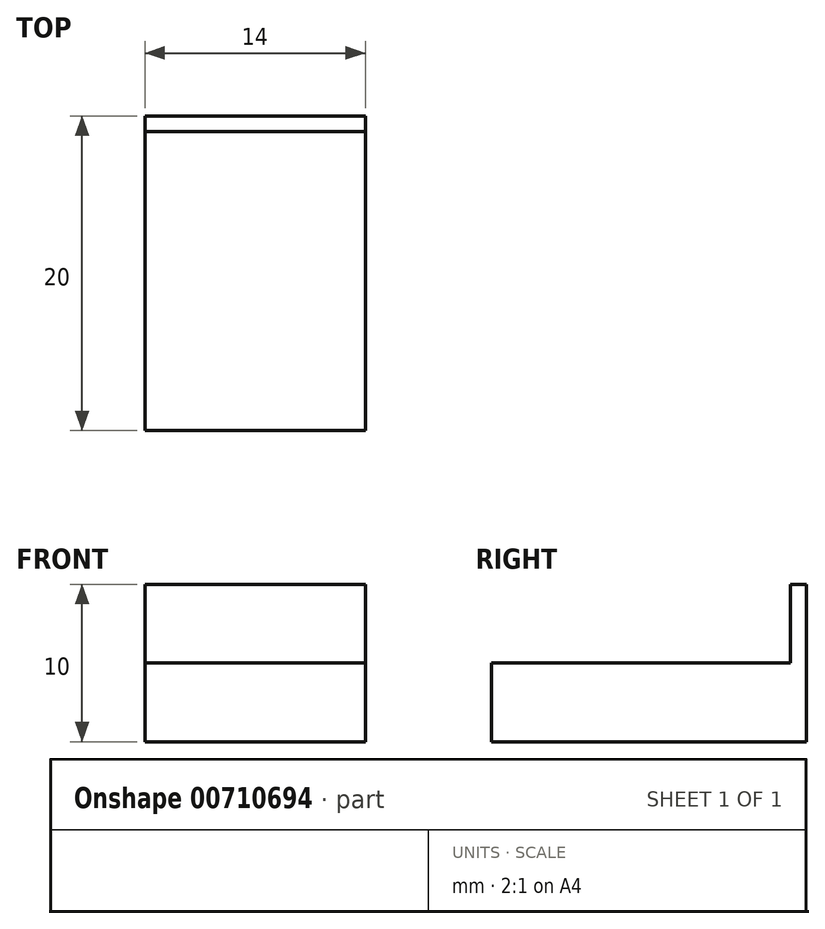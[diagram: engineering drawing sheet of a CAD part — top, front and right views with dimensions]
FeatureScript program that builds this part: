
annotation { "Feature Type Name" : "Feature", "Feature Type Description" : "" }
export const myFeature = defineFeature(function(context is Context, id is Id, definition is map)
    precondition{}
    {
        {
            var Q0;
            Q0=qCreatedBy(makeId("Top.planeOp"),FACE);
            var sketch = newSketch(context, id + "F0", { "sketchPlane" : qUnion([Q0])});
            skLineSegment(sketch, "E0.bottom", {"start": v(0, 0) * mm, "end": v(14, 0) * mm});
            skLineSegment(sketch, "E0.top", {"start": v(0, -20) * mm, "end": v(14, -20) * mm});
            skLineSegment(sketch, "E0.left", {"start": v(0, 0) * mm, "end": v(0, -20) * mm});
            skLineSegment(sketch, "E0.right", {"start": v(14, 0) * mm, "end": v(14, -20) * mm});
            skSolve(sketch);
        }
        {
            var Q0;
            Q0 = qSketchRegion(id + "F0", true);
            extrude(context, id + "F1", {"entities" : qUnion([Q0]), "depth" : 5 * mm, "offsetDistance" : 25 * mm});
        }
        {
            var Q0;
            Q0=qCreatedBy(makeId("Top.planeOp"),FACE);
            var sketch = newSketch(context, id + "F2", { "sketchPlane" : qUnion([Q0])});
            skLineSegment(sketch, "E1.bottom", {"start": v(0, 0) * mm, "end": v(14, 0) * mm});
            skLineSegment(sketch, "E1.top", {"start": v(0, -1) * mm, "end": v(14, -1) * mm});
            skLineSegment(sketch, "E1.left", {"start": v(0, 0) * mm, "end": v(0, -1) * mm});
            skLineSegment(sketch, "E1.right", {"start": v(14, 0) * mm, "end": v(14, -1) * mm});
            skSolve(sketch);
        }
        {
            var Q0;
            Q0 = qSketchRegion(id + "F2", true);
            extrude(context, id + "F3", {"entities" : qUnion([Q0]), "operationType" : NewBodyOperationType.ADD, "depth" : 10 * mm, "offsetDistance" : 25 * mm});
        }
    });
